# Revit family: TY3221
name_source: partatom
category: Sprinklers
revit_build: Autodesk Revit 2016 (Build: 20150220_1215(x64)
units: mm (PartAtom-declared; Revit-internal decimal feet)

## family parameters
Always vertical = Yes
Cut with Voids When Loaded = No
Maintain Annotation Orientation = No
OmniClass Number = 23.65.70.17.11.24
OmniClass Title = Fire Fighting Sprinkler Heads
Part Type = Normal
Room Calculation Point = No
Round Connector Dimension = Use Diameter
Shared = No
Work Plane-Based = No

## types (4) — shared parameters
COBie = Yes
COBie.Component.Name = Sprinklers:ESFR Pendent_Brass_SIN
COBie.Type = Yes
COBie.Type.AssetType = Fixed
COBie.Type.Category = Pr_70_55_97_84:Sprinklers
COBie.Type.DurationUnit = year
COBie.Type.Manufacturer = Tyco Fire Protection Products
COBie.Type.Material = Bronze
COBie.Type.Shape = Cylinder
COBie.Type.Size = 1/2"(DN15)
COBie.Type.WarrantyGuarantorParts = http://tycofsbp.com
Coverage = Standard
K-Factor = 79.9096
Manufacturer = Tyco Fire Protection Products
Manufacturer URL = www.tyco-fire.com
Model = TY-FRL
Nominal Diameter 1 = 15 mm
Orifice = Standard
Orifice Size = 0 mm
Outside Diameter 1 = 21 mm
Response = Quick
SIN No = TY3221
Takeout 1 = 68 mm
Technical Data Sheet No = TFP130
zero-valued in all types: COBie.Type.NominalHeight, COBie.Type.NominalLength, COBie.Type.NominalWidth, COBie.Type.ReplacementCost, Style Id

## per-type parameters (varying)
| type | COBie.Component.Description | COBie.Type.Colour | COBie.Type.Finish | COBie.Type.ModelNumber | COBie.Type.ModelReference | Part No | Temperature Rating |
| TY-FRL Pendent Brass 165°F/74°C 5.6K ½" NPT_58-982-1-165 | TY-FRL Wet Pendent  73.9°C K80 DN15 NPT Br | Yellow | Natural Brass | 58-982-1-165 | TY-FRL Wet Pendent  73.9°C K80 DN15 NPT Br | 58-982-1-165 | 74 °C |
| TY-FRL Pendent Brass 212°F/100°C 5.6K ½" NPT_58-982-1-212 | TY-FRL Wet Pendent  100°C K80 DN15 NPT Br | Yellow | Natural Brass | 58-982-1-212 | TY-FRL Wet Pendent  100°C K80 DN15 NPT Br | 58-982-1-212 | 100 °C |
| TY-FRL Pendent Chrome 165°F/74°C 5.6K ½" NPT_58-982-9-165 | TY-FRL Wet Pendent  73.9°C K80 DN15 NPT Chr | White | Chrome Plated | 58-982-9-165 | TY-FRL Wet Pendent  73.9°C K80 DN15 NPT Chr | 58-982-9-165 | 74 °C |
| TY-FRL Pendent Chrome 212°F/100°C 5.6K ½" NPT_58-982-9-212 | TY-FRL Wet Pendent  100°C K80 DN15 NPT Chr | White | Chrome Plated | 58-982-9-212 | TY-FRL Wet Pendent  100°C K80 DN15 NPT Chr | 58-982-9-212 | 100 °C |

note: column(s) folded — value = type name in every type: Description

## geometry (parser evidence)
native form markers: Blend x2, Sweep x50
no freeform markers — native parametric forms only
